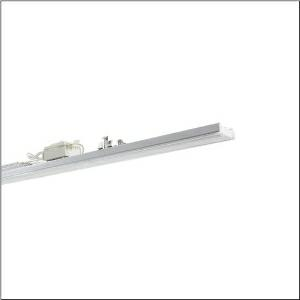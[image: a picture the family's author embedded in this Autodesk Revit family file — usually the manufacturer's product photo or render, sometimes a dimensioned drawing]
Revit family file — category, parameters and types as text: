
# Revit family: licross_11_recessed_mo_51te12cn49xg
name_source: partatom
category: Lighting Fixtures
units: mm (PartAtom-declared; Revit-internal decimal feet)

## family parameters
Cut with Voids When Loaded = No
Host = Face
Light Source = No
Part Type = Normal
Room Calculation Point = No
Round Connector Dimension = Use Diameter
Shared = No

## types (1)
- --- (1 x LED, 9310 lm, 49.3 W, 4000K)
    Apparent Load = 49 VA
    CIE Flux Codes = 67 92 99 100 100
    Color Rendering = 80
    Color Temperature = 4000K
    Default Elevation = 1800 mm
    Description = Licross 11 Recessed MO, luminaire insert, of sheet steel, galvanised, coil coated, white, length: 1.500mm, width: 66mm, height: 67mm, LED rated luminous flux: 9.310lm, light colour: 840, SDCM (Standard Deviation of Colour Matching)MacAdam ≤ 2 SDCM (initial), control gear: ON/OFF Multilumen, CLOi, with plug, 3-pole, with phase selection, mains connection: 220..240V, AC, 50/60Hz, start of lifetime: 49W, end of service life: 55W, internal wiring halogen-free, primary optical cover: cover, of PMMA, light emission: direct distribution, primary light characteristic: symmetric, protection rating (complete): IP54, insulation class (complete): insulation class I (protective earthing), certification: CE, ENEC, VDE, UKCA, protection symbol: D if used in an environment with non-conductive dust loads with corresponding accessories, impact resistance: IK06, permissible ambient temperature for indoor applications: -35..+40°C, corresponds to IFS (International Featured Standards) requirements for safety and quality in the food industry, reducing of maximum allowable ambient temperature of 5°C with ceiling mounting, LABS conformity tested according to VDMA 24364:2018-05, The light source and the operating device comply with the requirements of the Ecodesign Regulation (EU) 2019/2020 and are replaceable in accordance with this regulation, packaging unit: 1 piece
    Height = 58 mm
    Lamp = 1 x LED
    Lamp Light Flux = 9310 lm
    Lamp Power = 49.3 W
    Lamp count = 1
    Length = 1500 mm
    Luminous efficacy = 189 lm/W
    Manufacturer = Siteco
    ModVariant = No
    Model = 51TE12CN49XG
    Mounting Place = Ceiling
    Mounting Type = Pendant
    Number of Poles = 1
    OnlyDefault = Yes
    Power Factor = 1
    Product Name = Licross 11 Recessed MO
    Product group = luminaire insert | ceiling pendant
    ProductGroupID = 901
    Protection Class = Protection class I
    Protection Degree = IP 54
    RLX_Detail_Level = 1
    RLX_Emergency_Light_Flux = 0 lm
    RLX_Emergency_Type = 0
    RLX_Emergency_Type_DB = No
    RlxData = <blob elided: 22537 chars, md5=d4b4b732>
    Socket = socket
    Standby Power = 0 W
    System Light Flux = 9310 lm
    System Power = 49 W
    Type Comments = factory setting: luminous flux: 100 % | (A | C | E) | 113 mA
    Type Image = l_1296930.jpg
    URL = http://relux.com
    VarID = @adj_090883
    Voltage = 0 V
    Weight = 0.00 kg
    Width = 66 mm

## geometry (parser evidence)
native form markers: Blend x4, Sweep x10
no freeform markers — native parametric forms only
